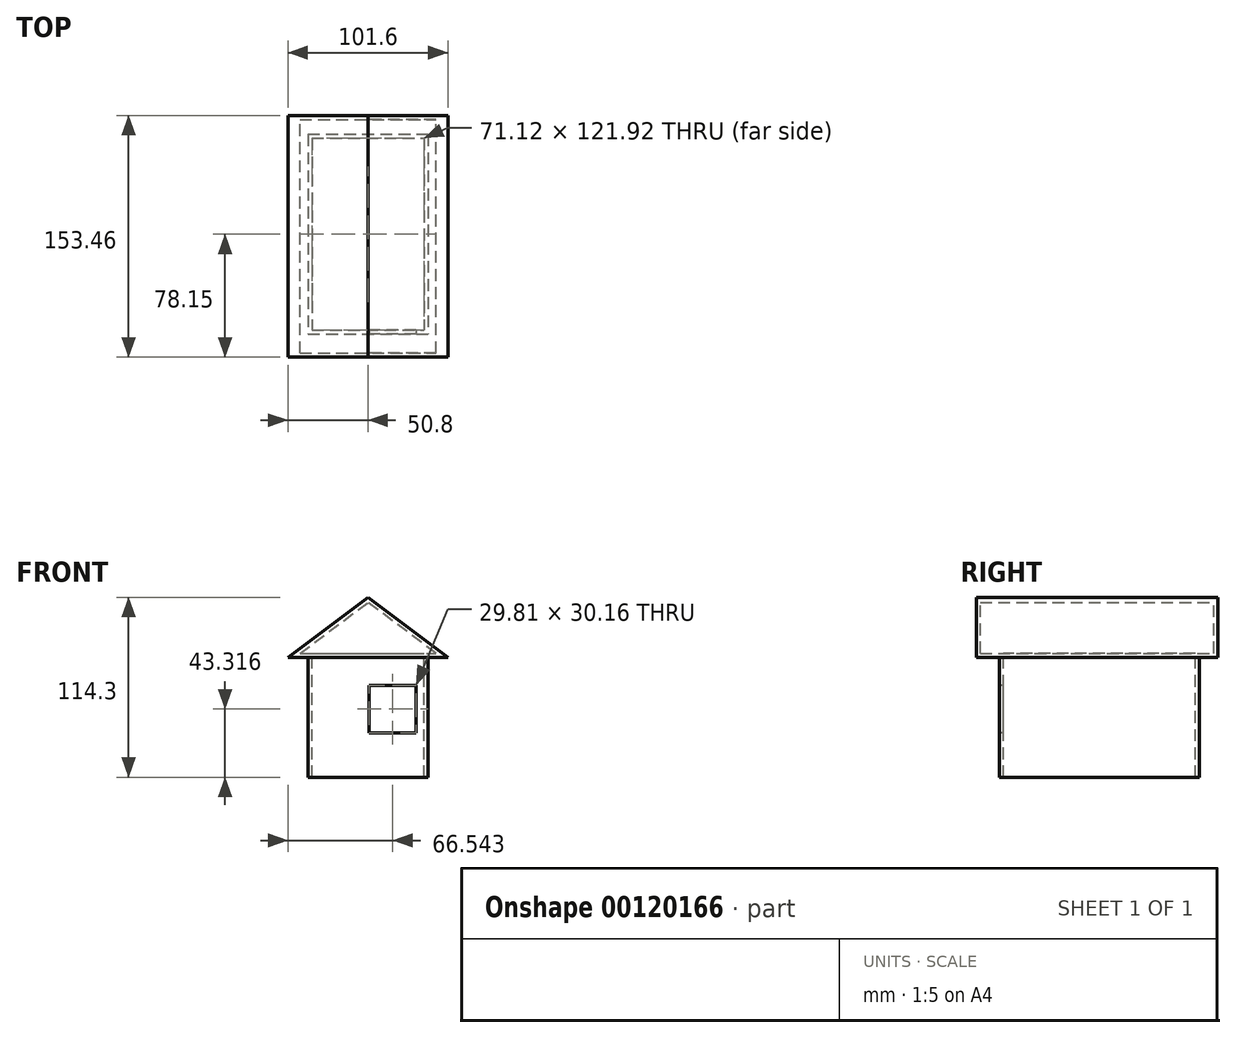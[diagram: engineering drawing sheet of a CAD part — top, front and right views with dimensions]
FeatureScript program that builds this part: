
annotation { "Feature Type Name" : "Feature", "Feature Type Description" : "" }
export const myFeature = defineFeature(function(context is Context, id is Id, definition is map)
    precondition{}
    {
        {
            var Q0;
            Q0=qCreatedBy(makeId("Front.planeOp"),FACE);
            var sketch = newSketch(context, id + "F0", { "sketchPlane" : qUnion([Q0])});
            skLineSegment(sketch, "E0.bottom", {"start": v(0, 0) * mm, "end": v(76.2, 0) * mm});
            skLineSegment(sketch, "E0.top", {"start": v(0, 76.2) * mm, "end": v(76.2, 76.2) * mm});
            skLineSegment(sketch, "E0.left", {"start": v(0, 0) * mm, "end": v(0, 76.2) * mm});
            skLineSegment(sketch, "E0.right", {"start": v(76.2, 0) * mm, "end": v(76.2, 76.2) * mm});
            skLineSegment(sketch, "E1.bottom", {"start": v(55.6, -18.98) * mm, "end": v(64.43, -18.98) * mm});
            skLineSegment(sketch, "E1.top", {"start": v(55.6, -52.81) * mm, "end": v(64.43, -52.81) * mm});
            skLineSegment(sketch, "E1.left", {"start": v(55.6, -18.98) * mm, "end": v(55.6, -52.81) * mm});
            skLineSegment(sketch, "E1.right", {"start": v(64.43, -18.98) * mm, "end": v(64.43, -52.81) * mm});
            skSolve(sketch);
        }
        {
            var Q0;
            Q0=makeQuery(id+"F0.imprint","IMPRINT",FACE,{"disambiguationData":[TD([[makeQuery(id+"F0.imprint","IMPRINT",EDGE,{"derivedFrom":sQuery(id+"F0.wireOp",EDGE,"E0.bottom")}),1.0]])]});
            extrude(context, id + "F1", {"entities" : qUnion([Q0]), "oppositeDirection" : true, "depth" : 127 * mm});
        }
        {
            var Q0;
            Q0=qCreatedBy(makeId("Front.planeOp"),FACE);
            var sketch = newSketch(context, id + "F2", { "sketchPlane" : qUnion([Q0])});
            skLineSegment(sketch, "E2.0", {"start": v(0, 76.2) * mm, "end": v(76.2, 76.2) * mm});
            skLineSegment(sketch, "E3", {"start": v(38.1, 76.2) * mm, "end": v(38.1, 114.3) * mm});
            skLineSegment(sketch, "E4", {"start": v(0, 76.2) * mm, "end": v(-12.7, 76.2) * mm});
            skLineSegment(sketch, "E5", {"start": v(76.2, 76.2) * mm, "end": v(88.9, 76.2) * mm});
            skLineSegment(sketch, "E6", {"start": v(88.9, 76.2) * mm, "end": v(38.1, 114.3) * mm});
            skLineSegment(sketch, "E7", {"start": v(-12.7, 76.2) * mm, "end": v(38.1, 114.3) * mm});
            skSolve(sketch);
        }
        {
            var Q0;
            {var subQ2=sQuery(id+"F2.wireOp",EDGE,"E3");Q0=makeQuery(id+"F2.imprint","IMPRINT",FACE,{"disambiguationData":[TD([[makeQuery(id+"F2.imprint","IMPRINT",EDGE,{"derivedFrom":subQ2}),-1.0]])]});}
            var Q1;
            {var subQ2=sQuery(id+"F2.wireOp",EDGE,"E3");Q1=makeQuery(id+"F2.imprint","IMPRINT",FACE,{"disambiguationData":[TD([[makeQuery(id+"F2.imprint","IMPRINT",EDGE,{"derivedFrom":subQ2}),1.0]])]});}
            extrude(context, id + "F3", {"entities" : qUnion([Q0, Q1]), "operationType" : NewBodyOperationType.ADD, "depth" : 14.65 * mm, "hasSecondDirection" : true, "secondDirectionOppositeDirection" : true, "secondDirectionDepth" : 138.8 * mm});
        }
        {
            var Q0;
            Q0=makeQuery(id+"F1.opExtrude","SWEPT_FACE",FACE,{"disambiguationData":[OSD([sQuery(id+"F0.wireOp",EDGE,"E0.bottom")])]});
            shell(context, id + "F4", {"entities" : qUnion([Q0]), "thickness" : 2.54 * mm});
        }
        {
            var Q0;
            Q0=qCreatedBy(makeId("Front.planeOp"),FACE);
            var sketch = newSketch(context, id + "F5", { "sketchPlane" : qUnion([Q0])});
            skLineSegment(sketch, "E8.0", {"start": v(0, 0) * mm, "end": v(76.2, 0) * mm});
            skSolve(sketch);
        }
        {
            var Q0;
            Q0=qCreatedBy(makeId("Front.planeOp"),FACE);
            var sketch = newSketch(context, id + "F6", { "sketchPlane" : qUnion([Q0])});
            skLineSegment(sketch, "E9.0", {"start": v(0, 0) * mm, "end": v(76.2, 0) * mm});
            skLineSegment(sketch, "E10.bottom", {"start": v(4.27, 0) * mm, "end": v(32.7, 0) * mm});
            skLineSegment(sketch, "E10.top", {"start": v(4.27, 48.69) * mm, "end": v(32.7, 48.69) * mm});
            skLineSegment(sketch, "E10.left", {"start": v(4.27, 0) * mm, "end": v(4.27, 48.69) * mm});
            skLineSegment(sketch, "E10.right", {"start": v(32.7, 0) * mm, "end": v(32.7, 48.69) * mm});
            skLineSegment(sketch, "E11.bottom", {"start": v(68.75, 28.24) * mm, "end": v(38.94, 28.24) * mm});
            skLineSegment(sketch, "E11.top", {"start": v(68.75, 58.4) * mm, "end": v(38.94, 58.4) * mm});
            skLineSegment(sketch, "E11.left", {"start": v(68.75, 28.24) * mm, "end": v(68.75, 58.4) * mm});
            skLineSegment(sketch, "E11.right", {"start": v(38.94, 28.24) * mm, "end": v(38.94, 58.4) * mm});
            skSolve(sketch);
        }
        {
            var Q0;
            Q0=makeQuery(id+"F6.imprint","IMPRINT",FACE,{"disambiguationData":[TD([[makeQuery(id+"F6.imprint","IMPRINT",EDGE,{"derivedFrom":sQuery(id+"F6.wireOp",EDGE,"E11.bottom")}),-1.0]])]});
            var Q1;
            Q1=makeQuery(id+"F6.imprint","IMPRINT",FACE,{"disambiguationData":[TD([[makeQuery(id+"F6.imprint","IMPRINT",EDGE,{"derivedFrom":sQuery(id+"F6.wireOp",EDGE,"E10.bottom")}),1.0]])]});
            extrude(context, id + "F7", {"entities" : qUnion([Q0, Q1]), "operationType" : NewBodyOperationType.REMOVE, "oppositeDirection" : true, "depth" : 25.4 * mm});
        }
    });
